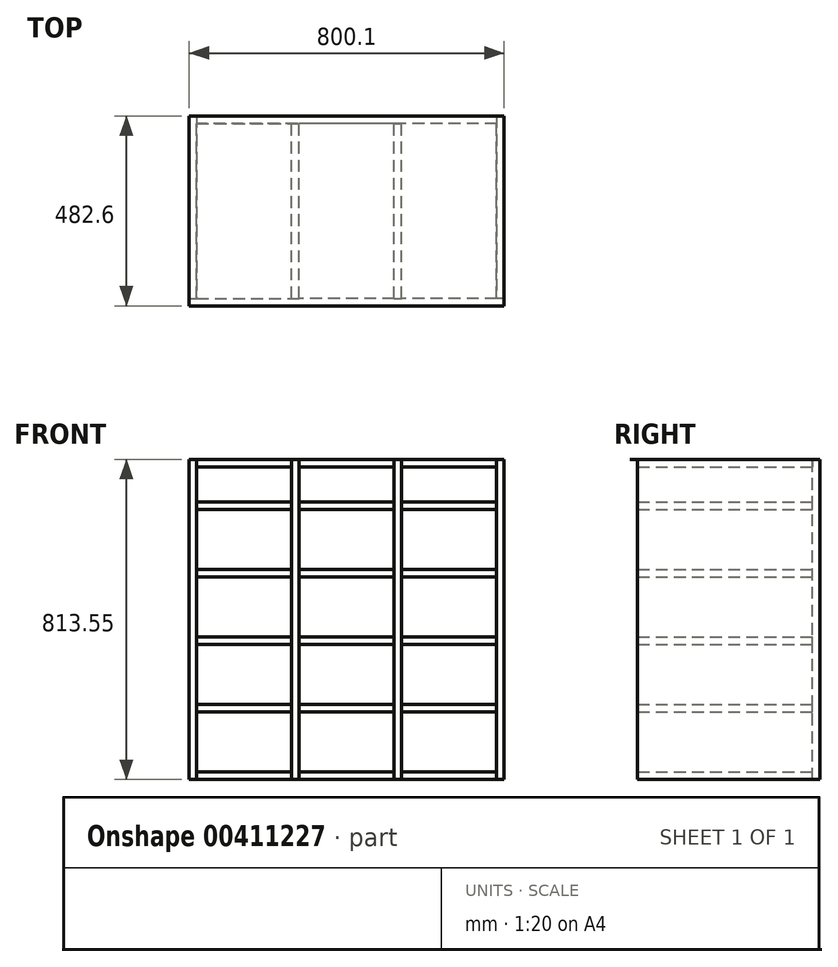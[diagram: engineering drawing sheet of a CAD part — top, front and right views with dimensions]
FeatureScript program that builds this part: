
annotation { "Feature Type Name" : "Feature", "Feature Type Description" : "" }
export const myFeature = defineFeature(function(context is Context, id is Id, definition is map)
    precondition{}
    {
        {
            assignVariable(context, id + "F0", {"name" : "plywood", "anyValue" : .75});
        }
        {
            var Q0;
            Q0=qCreatedBy(makeId("Top.planeOp"),FACE);
            var sketch = newSketch(context, id + "F1", { "sketchPlane" : qUnion([Q0])});
            skLineSegment(sketch, "E0.bottom", {"start": v(400.05, 241.3) * mm, "end": v(-400.05, 241.3) * mm});
            skLineSegment(sketch, "E0.top", {"start": v(400.05, -241.3) * mm, "end": v(-400.05, -241.3) * mm});
            skLineSegment(sketch, "E0.left", {"start": v(400.05, 241.3) * mm, "end": v(400.05, -241.3) * mm});
            skLineSegment(sketch, "E0.right", {"start": v(-400.05, 241.3) * mm, "end": v(-400.05, -241.3) * mm});
            skPoint(sketch, "E0.middle", {"position": v(0, 0) * mm});
            skLineSegment(sketch, "E1", {"start": v(0, 241.3) * mm, "end": v(0, -241.3) * mm, "construction": true});
            skSolve(sketch);
        }
        {
            var Q0;
            Q0=makeQuery(id+"F1.imprint","IMPRINT",FACE,{"disambiguationData":[TD([[makeQuery(id+"F1.imprint","IMPRINT",EDGE,{"derivedFrom":sQuery(id+"F1.wireOp",EDGE,"E0.bottom")}),1.0]])]});
            extrude(context, id + "F2", {"entities" : qUnion([Q0]), "depth" : (getVariable(context, 'plywood')) * mm});
        }
        {
            var Q0;
            Q0=makeQuery(id+"F1.imprint","IMPRINT",FACE,{"disambiguationData":[TD([[makeQuery(id+"F1.imprint","IMPRINT",EDGE,{"derivedFrom":sQuery(id+"F1.wireOp",EDGE,"E0.bottom")}),1.0]])]});
            var sketch = newSketch(context, id + "F3", { "sketchPlane" : qUnion([Q0])});
            skLineSegment(sketch, "E2.bottom", {"start": v(-400.05, 241.3) * mm, "end": v(-381, 241.3) * mm});
            skLineSegment(sketch, "E2.top", {"start": v(-400.05, -222.25) * mm, "end": v(-381, -222.25) * mm});
            skLineSegment(sketch, "E2.left", {"start": v(-400.05, 241.3) * mm, "end": v(-400.05, -222.25) * mm});
            skLineSegment(sketch, "E2.right", {"start": v(-381, 241.3) * mm, "end": v(-381, -222.25) * mm});
            skLineSegment(sketch, "E3.bottom", {"start": v(400.05, 241.3) * mm, "end": v(381, 241.3) * mm});
            skLineSegment(sketch, "E3.top", {"start": v(400.05, -222.25) * mm, "end": v(381, -222.25) * mm});
            skLineSegment(sketch, "E3.left", {"start": v(400.05, 241.3) * mm, "end": v(400.05, -222.25) * mm});
            skLineSegment(sketch, "E3.right", {"start": v(381, 241.3) * mm, "end": v(381, -222.25) * mm});
            skSolve(sketch);
        }
        {
            var Q0;
            Q0=qSketchRegion(id+"F3",true);
            extrude(context, id + "F4", {"entities" : qUnion([Q0]), "oppositeDirection" : true, "depth" : 812.8 * mm});
        }
        {
            var Q0;
            Q0=makeQuery(id+"F1.imprint","IMPRINT",FACE,{"disambiguationData":[TD([[makeQuery(id+"F1.imprint","IMPRINT",EDGE,{"derivedFrom":sQuery(id+"F1.wireOp",EDGE,"E0.bottom")}),1.0]])]});
            var sketch = newSketch(context, id + "F5", { "sketchPlane" : qUnion([Q0])});
            skLineSegment(sketch, "E4.bottom", {"start": v(381, 241.3) * mm, "end": v(-381, 241.3) * mm});
            skLineSegment(sketch, "E4.top", {"start": v(381, 222.25) * mm, "end": v(-381, 222.25) * mm});
            skLineSegment(sketch, "E4.left", {"start": v(381, 241.3) * mm, "end": v(381, 222.25) * mm});
            skLineSegment(sketch, "E4.right", {"start": v(-381, 241.3) * mm, "end": v(-381, 222.25) * mm});
            skPoint(sketch, "E4.middle", {"position": v(0, 231.77) * mm});
            skSolve(sketch);
        }
        {
            var Q0;
            Q0=qSketchRegion(id+"F5",true);
            extrude(context, id + "F6", {"entities" : qUnion([Q0]), "oppositeDirection" : true, "depth" : 812.8 * mm});
        }
        {
            var Q0;
            Q0=makeQuery(id+"F1.imprint","IMPRINT",FACE,{"disambiguationData":[TD([[makeQuery(id+"F1.imprint","IMPRINT",EDGE,{"derivedFrom":sQuery(id+"F1.wireOp",EDGE,"E0.bottom")}),1.0]])]});
            var sketch = newSketch(context, id + "F7", { "sketchPlane" : qUnion([Q0])});
            skLineSegment(sketch, "E5.bottom", {"start": v(-139.7, -222.25) * mm, "end": v(-120.65, -222.25) * mm});
            skLineSegment(sketch, "E5.top", {"start": v(-139.7, 222.25) * mm, "end": v(-120.65, 222.25) * mm});
            skLineSegment(sketch, "E5.left", {"start": v(-139.7, -222.25) * mm, "end": v(-139.7, 222.25) * mm});
            skLineSegment(sketch, "E5.right", {"start": v(-120.65, -222.25) * mm, "end": v(-120.65, 222.25) * mm});
            skLineSegment(sketch, "E6.bottom", {"start": v(120.65, -222.25) * mm, "end": v(139.7, -222.25) * mm});
            skLineSegment(sketch, "E6.top", {"start": v(120.65, 222.25) * mm, "end": v(139.7, 222.25) * mm});
            skLineSegment(sketch, "E6.left", {"start": v(120.65, -222.25) * mm, "end": v(120.65, 222.25) * mm});
            skLineSegment(sketch, "E6.right", {"start": v(139.7, -222.25) * mm, "end": v(139.7, 222.25) * mm});
            skSolve(sketch);
        }
        {
            var Q0;
            Q0=qSketchRegion(id+"F7",true);
            extrude(context, id + "F8", {"entities" : qUnion([Q0]), "oppositeDirection" : true, "depth" : 812.8 * mm});
        }
        {
            var Q0;
            Q0=makeQuery(id+"F6.opExtrude","SWEPT_FACE",FACE,{"disambiguationData":[OSD([sQuery(id+"F5.wireOp",EDGE,"E4.top")])]});
            var sketch = newSketch(context, id + "F9", { "sketchPlane" : qUnion([Q0])});
            skLineSegment(sketch, "E7.bottom", {"start": v(-139.7, -19.05) * mm, "end": v(-381, -19.05) * mm});
            skLineSegment(sketch, "E7.top", {"start": v(-139.7, 0) * mm, "end": v(-381, 0) * mm});
            skLineSegment(sketch, "E7.left", {"start": v(-139.7, -19.05) * mm, "end": v(-139.7, 0) * mm});
            skLineSegment(sketch, "E7.right", {"start": v(-381, -19.05) * mm, "end": v(-381, 0) * mm});
            skLineSegment(sketch, "E8.bottom", {"start": v(139.7, -19.05) * mm, "end": v(381, -19.05) * mm});
            skLineSegment(sketch, "E8.top", {"start": v(139.7, 0) * mm, "end": v(381, 0) * mm});
            skLineSegment(sketch, "E8.left", {"start": v(139.7, -19.05) * mm, "end": v(139.7, 0) * mm});
            skLineSegment(sketch, "E8.right", {"start": v(381, -19.05) * mm, "end": v(381, 0) * mm});
            skLineSegment(sketch, "E9.bottom", {"start": v(120.65, 0) * mm, "end": v(-120.65, 0) * mm});
            skLineSegment(sketch, "E9.top", {"start": v(120.65, -19.05) * mm, "end": v(-120.65, -19.05) * mm});
            skLineSegment(sketch, "E9.left", {"start": v(120.65, 0) * mm, "end": v(120.65, -19.05) * mm});
            skLineSegment(sketch, "E9.right", {"start": v(-120.65, 0) * mm, "end": v(-120.65, -19.05) * mm});
            skPoint(sketch, "E9.middle", {"position": v(0, -9.53) * mm});
            skLineSegment(sketch, "E10.bottom", {"start": v(-381, -793.75) * mm, "end": v(-139.7, -793.75) * mm});
            skLineSegment(sketch, "E10.top", {"start": v(-381, -812.8) * mm, "end": v(-139.7, -812.8) * mm});
            skLineSegment(sketch, "E10.left", {"start": v(-381, -793.75) * mm, "end": v(-381, -812.8) * mm});
            skLineSegment(sketch, "E10.right", {"start": v(-139.7, -793.75) * mm, "end": v(-139.7, -812.8) * mm});
            skLineSegment(sketch, "E11.bottom", {"start": v(381, -793.75) * mm, "end": v(139.7, -793.75) * mm});
            skLineSegment(sketch, "E11.top", {"start": v(381, -812.8) * mm, "end": v(139.7, -812.8) * mm});
            skLineSegment(sketch, "E11.left", {"start": v(381, -793.75) * mm, "end": v(381, -812.8) * mm});
            skLineSegment(sketch, "E11.right", {"start": v(139.7, -793.75) * mm, "end": v(139.7, -812.8) * mm});
            skLineSegment(sketch, "E12.bottom", {"start": v(120.65, -812.8) * mm, "end": v(-120.65, -812.8) * mm});
            skLineSegment(sketch, "E12.top", {"start": v(120.65, -793.75) * mm, "end": v(-120.65, -793.75) * mm});
            skLineSegment(sketch, "E12.left", {"start": v(120.65, -812.8) * mm, "end": v(120.65, -793.75) * mm});
            skLineSegment(sketch, "E12.right", {"start": v(-120.65, -812.8) * mm, "end": v(-120.65, -793.75) * mm});
            skPoint(sketch, "E12.middle", {"position": v(0, -803.27) * mm});
            skLineSegment(sketch, "E13.0.1.0", {"start": v(139.7, -622.3) * mm, "end": v(139.7, -641.35) * mm});
            skLineSegment(sketch, "E13.0.1.1", {"start": v(-139.7, -622.3) * mm, "end": v(-139.7, -641.35) * mm});
            skLineSegment(sketch, "E13.0.1.2", {"start": v(-381, -622.3) * mm, "end": v(-381, -641.35) * mm});
            skLineSegment(sketch, "E13.0.1.3", {"start": v(381, -641.35) * mm, "end": v(139.7, -641.35) * mm});
            skLineSegment(sketch, "E13.0.1.4", {"start": v(120.65, -641.35) * mm, "end": v(-120.65, -641.35) * mm});
            skLineSegment(sketch, "E13.0.1.5", {"start": v(120.65, -641.35) * mm, "end": v(120.65, -622.3) * mm});
            skLineSegment(sketch, "E13.0.1.6", {"start": v(120.65, -622.3) * mm, "end": v(-120.65, -622.3) * mm});
            skLineSegment(sketch, "E13.0.1.7", {"start": v(-381, -622.3) * mm, "end": v(-139.7, -622.3) * mm});
            skLineSegment(sketch, "E13.0.1.8", {"start": v(381, -622.3) * mm, "end": v(381, -641.35) * mm});
            skLineSegment(sketch, "E13.0.1.9", {"start": v(-381, -641.35) * mm, "end": v(-139.7, -641.35) * mm});
            skLineSegment(sketch, "E13.0.1.10", {"start": v(-120.65, -641.35) * mm, "end": v(-120.65, -622.3) * mm});
            skLineSegment(sketch, "E13.0.1.11", {"start": v(381, -622.3) * mm, "end": v(139.7, -622.3) * mm});
            skLineSegment(sketch, "E13.0.2.0", {"start": v(139.7, -450.85) * mm, "end": v(139.7, -469.9) * mm});
            skLineSegment(sketch, "E13.0.2.1", {"start": v(-139.7, -450.85) * mm, "end": v(-139.7, -469.9) * mm});
            skLineSegment(sketch, "E13.0.2.2", {"start": v(-381, -450.85) * mm, "end": v(-381, -469.9) * mm});
            skLineSegment(sketch, "E13.0.2.3", {"start": v(381, -469.9) * mm, "end": v(139.7, -469.9) * mm});
            skLineSegment(sketch, "E13.0.2.4", {"start": v(120.65, -469.9) * mm, "end": v(-120.65, -469.9) * mm});
            skLineSegment(sketch, "E13.0.2.5", {"start": v(120.65, -469.9) * mm, "end": v(120.65, -450.85) * mm});
            skLineSegment(sketch, "E13.0.2.6", {"start": v(120.65, -450.85) * mm, "end": v(-120.65, -450.85) * mm});
            skLineSegment(sketch, "E13.0.2.7", {"start": v(-381, -450.85) * mm, "end": v(-139.7, -450.85) * mm});
            skLineSegment(sketch, "E13.0.2.8", {"start": v(381, -450.85) * mm, "end": v(381, -469.9) * mm});
            skLineSegment(sketch, "E13.0.2.9", {"start": v(-381, -469.9) * mm, "end": v(-139.7, -469.9) * mm});
            skLineSegment(sketch, "E13.0.2.10", {"start": v(-120.65, -469.9) * mm, "end": v(-120.65, -450.85) * mm});
            skLineSegment(sketch, "E13.0.2.11", {"start": v(381, -450.85) * mm, "end": v(139.7, -450.85) * mm});
            skLineSegment(sketch, "E13.0.3.0", {"start": v(139.7, -279.4) * mm, "end": v(139.7, -298.45) * mm});
            skLineSegment(sketch, "E13.0.3.1", {"start": v(-139.7, -279.4) * mm, "end": v(-139.7, -298.45) * mm});
            skLineSegment(sketch, "E13.0.3.2", {"start": v(-381, -279.4) * mm, "end": v(-381, -298.45) * mm});
            skLineSegment(sketch, "E13.0.3.3", {"start": v(381, -298.45) * mm, "end": v(139.7, -298.45) * mm});
            skLineSegment(sketch, "E13.0.3.4", {"start": v(120.65, -298.45) * mm, "end": v(-120.65, -298.45) * mm});
            skLineSegment(sketch, "E13.0.3.5", {"start": v(120.65, -298.45) * mm, "end": v(120.65, -279.4) * mm});
            skLineSegment(sketch, "E13.0.3.6", {"start": v(120.65, -279.4) * mm, "end": v(-120.65, -279.4) * mm});
            skLineSegment(sketch, "E13.0.3.7", {"start": v(-381, -279.4) * mm, "end": v(-139.7, -279.4) * mm});
            skLineSegment(sketch, "E13.0.3.8", {"start": v(381, -279.4) * mm, "end": v(381, -298.45) * mm});
            skLineSegment(sketch, "E13.0.3.9", {"start": v(-381, -298.45) * mm, "end": v(-139.7, -298.45) * mm});
            skLineSegment(sketch, "E13.0.3.10", {"start": v(-120.65, -298.45) * mm, "end": v(-120.65, -279.4) * mm});
            skLineSegment(sketch, "E13.0.3.11", {"start": v(381, -279.4) * mm, "end": v(139.7, -279.4) * mm});
            skLineSegment(sketch, "E13.direction1", {"start": v(-381, -812.8) * mm, "end": v(-355.6, -812.8) * mm, "construction": true});
            skLineSegment(sketch, "E13.direction2", {"start": v(-381, -812.8) * mm, "end": v(-381, -641.35) * mm, "construction": true});
            skLineSegment(sketch, "E14.0.0.4", {"start": v(139.7, -107.95) * mm, "end": v(139.7, -127) * mm});
            skLineSegment(sketch, "E14.3.0.4", {"start": v(-139.7, -107.95) * mm, "end": v(-139.7, -127) * mm});
            skLineSegment(sketch, "E14.6.0.4", {"start": v(-381, -107.95) * mm, "end": v(-381, -127) * mm});
            skLineSegment(sketch, "E14.9.0.4", {"start": v(381, -127) * mm, "end": v(139.7, -127) * mm});
            skLineSegment(sketch, "E14.12.0.4", {"start": v(120.65, -127) * mm, "end": v(-120.65, -127) * mm});
            skLineSegment(sketch, "E14.15.0.4", {"start": v(120.65, -127) * mm, "end": v(120.65, -107.95) * mm});
            skLineSegment(sketch, "E14.18.0.4", {"start": v(120.65, -107.95) * mm, "end": v(-120.65, -107.95) * mm});
            skLineSegment(sketch, "E14.21.0.4", {"start": v(-381, -107.95) * mm, "end": v(-139.7, -107.95) * mm});
            skLineSegment(sketch, "E14.24.0.4", {"start": v(381, -107.95) * mm, "end": v(381, -127) * mm});
            skLineSegment(sketch, "E14.27.0.4", {"start": v(-381, -127) * mm, "end": v(-139.7, -127) * mm});
            skLineSegment(sketch, "E14.30.0.4", {"start": v(-120.65, -127) * mm, "end": v(-120.65, -107.95) * mm});
            skLineSegment(sketch, "E14.33.0.4", {"start": v(381, -107.95) * mm, "end": v(139.7, -107.95) * mm});
            skSolve(sketch);
        }
        {
            var Q0;
            Q0 = qSketchRegion(id + "F9", true);
            var Q1;
            Q1=makeQuery(id+"F4.opExtrude","SWEPT_FACE",FACE,{"disambiguationData":[OSD([sQuery(id+"F3.wireOp",EDGE,"E2.top")])]});
            extrude(context, id + "F10", {"entities" : qUnion([Q0]), "endBound" : BoundingType.UP_TO_SURFACE, "endBoundEntityFace" : qUnion([Q1]), "depth" : 25.4 * mm});
        }
    });
